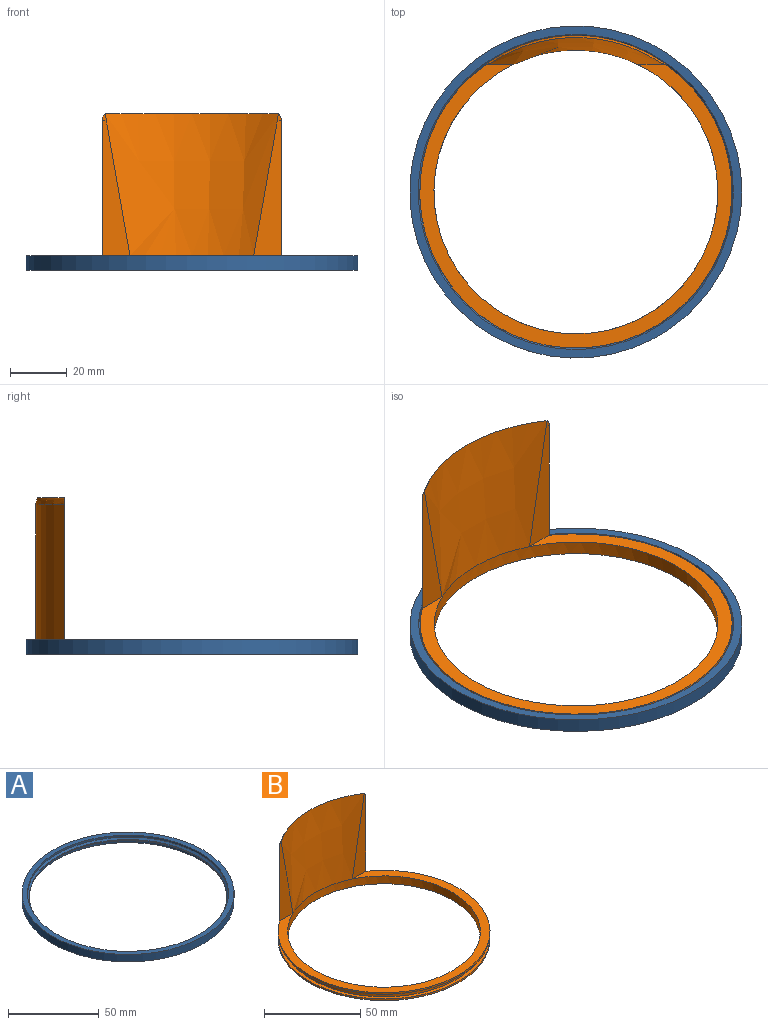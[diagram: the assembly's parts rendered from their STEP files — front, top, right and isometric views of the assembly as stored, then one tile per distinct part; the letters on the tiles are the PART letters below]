
ASSEMBLY  parts=2 mates=1
PART A: 8 faces, bbox 117x117x5 mm
  f0: cylinder r=55.5mm len=111mm, axis (0,0,-1), area 435.9mm2, adj f2,f6
  f1: cylinder r=58.5mm len=117mm, axis (0,0,-1), area 1837.8mm2, adj f2,f5
  f2: plane 117x117mm, normal (0,0,-1), area 1074.4mm2, adj f0,f1
  f3: cylinder r=54.5mm len=109mm, axis (0,0,-1), area 171.2mm2, adj f6,f7
  f4: cylinder r=55.5mm len=111mm, axis (0,0,-1), area 435.9mm2, adj f5,f7
  f5: plane 117x117mm, normal (0,0,1), area 1074.4mm2, adj f1,f4
  f6: cone r=55.5mm half-angle=45deg, axis (0,0,-1), area 488.7mm2, adj f0,f3
  f7: cone r=54.5mm half-angle=45deg, axis (0,0,1), area 488.7mm2, adj f3,f4
PART B: 12 faces, bbox 110x114.5x56.1 mm
  f0: cylinder r=50mm len=100mm, axis (0,0,-1), area 1570.8mm2, adj f3,f6,f10
  f1: cylinder r=55mm len=110mm, axis (0,0,-1), area 345.6mm2, adj f2,f3
  f2: plane 110x110mm, normal (0,0,1), area 678.6mm2, adj f1,f4
  f3: plane 110x110mm, normal (0,0,-1), area 1649.3mm2, adj f0,f1
  f4: cylinder r=53mm len=106mm, axis (0,0,-1), area 999mm2, adj f2,f7
  f5: cylinder r=55mm len=110mm, axis (0,0,-1), area 3551.5mm2, adj f6,f7,f8,f9,f11
  f6: plane 110x100mm, normal (0,0,1), area 1366.2mm2, adj f0,f5,f8,f9
  f7: plane 110x110mm, normal (0,0,-1), area 678.6mm2, adj f4,f5
  f8: plane 50x9.83mm, normal (0,-1,0), area 263.3mm2, adj f5,f6,f10,f11
  f9: plane 50x9.83mm, normal (0,-1,0), area 263.3mm2, adj f5,f6,f10,f11
  f10: cone r=50mm half-angle=5deg, axis (0,0,1), area 2774.2mm2, adj f0,f8,f9,f11
  f11: torus R=50mm, axis (0,0,1), area 168.2mm2, adj f5,f8,f9,f10
PLACE A t=(48.22,36.69,10.78)mm
PLACE B t=(48.22,36.69,10.78)mm
MATE revolute B.f0 <-> A.f0  axis (0,0,1) through (48.22,36.69,15.78)mm
